# Revit family: AFX-Gemini-LED_Pendant
name_source: partatom
category: Lighting Fixtures
units: mm (PartAtom-declared; Revit-internal decimal feet)

## family parameters
Cut with Voids When Loaded = No
Host = Face
Light Source = Yes
Part Type = Normal
Room Calculation Point = No
Round Connector Dimension = Use Diameter
Shared = No

## types (2) — shared parameters
Apparent Load = 0 VA
Assembly Code = D5020200
Body Finish = AFX - Black Steel
Cable Finish = AFX - Black Steel
Color Filter = 16777215
Colour Rendering Index = 90
Default Elevation = 48"
Diffuser Finish = AFX - White Acrylic
Dimming Lamp Color Temperature Shift = <None>
Emit Shape Visible in Rendering = No
Emit from Rectangle Length = 17 3/4"
Emit from Rectangle Width = 1 7/16"
Height = 4"
Housing Finish = AFX - Black Steel
Keynote = 12500
Manufacturer = AFX Inc
Product Documentation Link = https://www.afxinc.com
Revit File Built By = https://servex-us.com
Sustainability = https://lamprecycle.org
Tilt Angle = 90.00°
Type Comments = Gemini
URL = https://www.afxinc.com
Voltage = 120 V

## per-type parameters (varying)
| type | Description | Diameter | Diameter Housing | Heigth Housing | Photometric Web File | Wattage Comments |
| GEMP24LAJUDBK | LED Pendant Round - 24"Dia x 4"H | 24" | 5 29/32" | 1 25/32" | GEM24LAJUDBK_3000K_IES.IES | 45W |
| GEMP32LAJUDBK | LED Pendant Round - 36"Dia x 4"H | 36" | 11 1/32" | 1 3/16" | GEM32LAJUDNP_3000K_IES.IES | 60W |

note: column(s) folded — value = type name in every type: Model

## geometry (parser evidence)
native form markers: Sweep x4
no freeform markers — native parametric forms only
